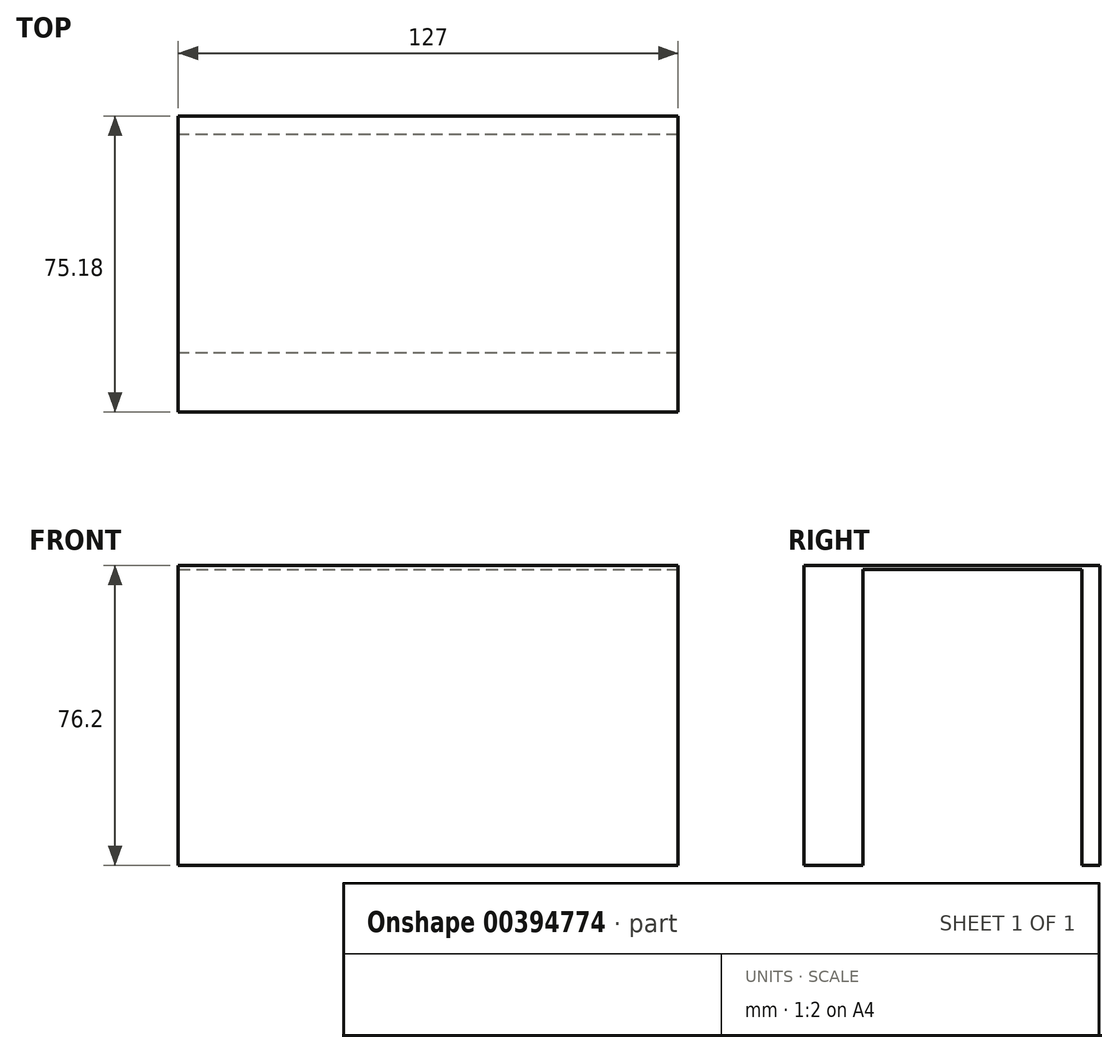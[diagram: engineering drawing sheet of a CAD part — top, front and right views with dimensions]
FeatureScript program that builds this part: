
annotation { "Feature Type Name" : "Feature", "Feature Type Description" : "" }
export const myFeature = defineFeature(function(context is Context, id is Id, definition is map)
    precondition{}
    {
        {
            var Q0;
            Q0=qCreatedBy(makeId("Front.planeOp"),FACE);
            var sketch = newSketch(context, id + "F0", { "sketchPlane" : qUnion([Q0])});
            skLineSegment(sketch, "E0.bottom", {"start": v(0, 23.26) * mm, "end": v(127, 23.26) * mm});
            skLineSegment(sketch, "E0.top", {"start": v(0, 99.46) * mm, "end": v(127, 99.46) * mm});
            skLineSegment(sketch, "E0.left", {"start": v(0, 23.26) * mm, "end": v(0, 99.46) * mm});
            skLineSegment(sketch, "E0.right", {"start": v(127, 23.26) * mm, "end": v(127, 99.46) * mm});
            skLineSegment(sketch, "E1.bottom", {"start": v(72.84, 23.26) * mm, "end": v(63.5, 23.26) * mm});
            skLineSegment(sketch, "E1.top", {"start": v(72.84, 23.26) * mm, "end": v(63.5, 23.26) * mm});
            skLineSegment(sketch, "E1.left", {"start": v(72.84, 23.26) * mm, "end": v(72.84, 23.26) * mm});
            skLineSegment(sketch, "E1.right", {"start": v(63.5, 23.26) * mm, "end": v(63.5, 23.26) * mm});
            skSolve(sketch);
        }
        {
            var Q0;
            Q0=makeQuery(id+"F0.imprint","IMPRINT",FACE,{"disambiguationData":[TD([[makeQuery(id+"F0.imprint","IMPRINT",EDGE,{"derivedFrom":sQuery(id+"F0.wireOp",EDGE,"E0.top")}),-1.0]])]});
            extrude(context, id + "F1", {"entities" : qUnion([Q0]), "oppositeDirection" : true, "depth" : 75.18 * mm});
        }
        {
            var Q0;
            Q0=makeQuery(id+"F1.opExtrude","SWEPT_FACE",FACE,{"disambiguationData":[OSD([sQuery(id+"F0.wireOp",EDGE,"E0.right")])]});
            var sketch = newSketch(context, id + "F2", { "sketchPlane" : qUnion([Q0])});
            skLineSegment(sketch, "E2.bottom", {"start": v(14.97, 98.5) * mm, "end": v(70.53, 98.5) * mm});
            skLineSegment(sketch, "E2.top", {"start": v(14.97, 22.3) * mm, "end": v(70.53, 22.3) * mm});
            skLineSegment(sketch, "E2.left", {"start": v(14.97, 98.5) * mm, "end": v(14.97, 22.3) * mm});
            skLineSegment(sketch, "E2.right", {"start": v(70.53, 98.5) * mm, "end": v(70.53, 22.3) * mm});
            skSolve(sketch);
        }
        {
            var Q0;
            Q0 = qSketchRegion(id + "F2", true);
            extrude(context, id + "F3", {"entities" : qUnion([Q0]), "operationType" : NewBodyOperationType.REMOVE, "oppositeDirection" : true, "depth" : 166.88 * mm});
        }
    });
